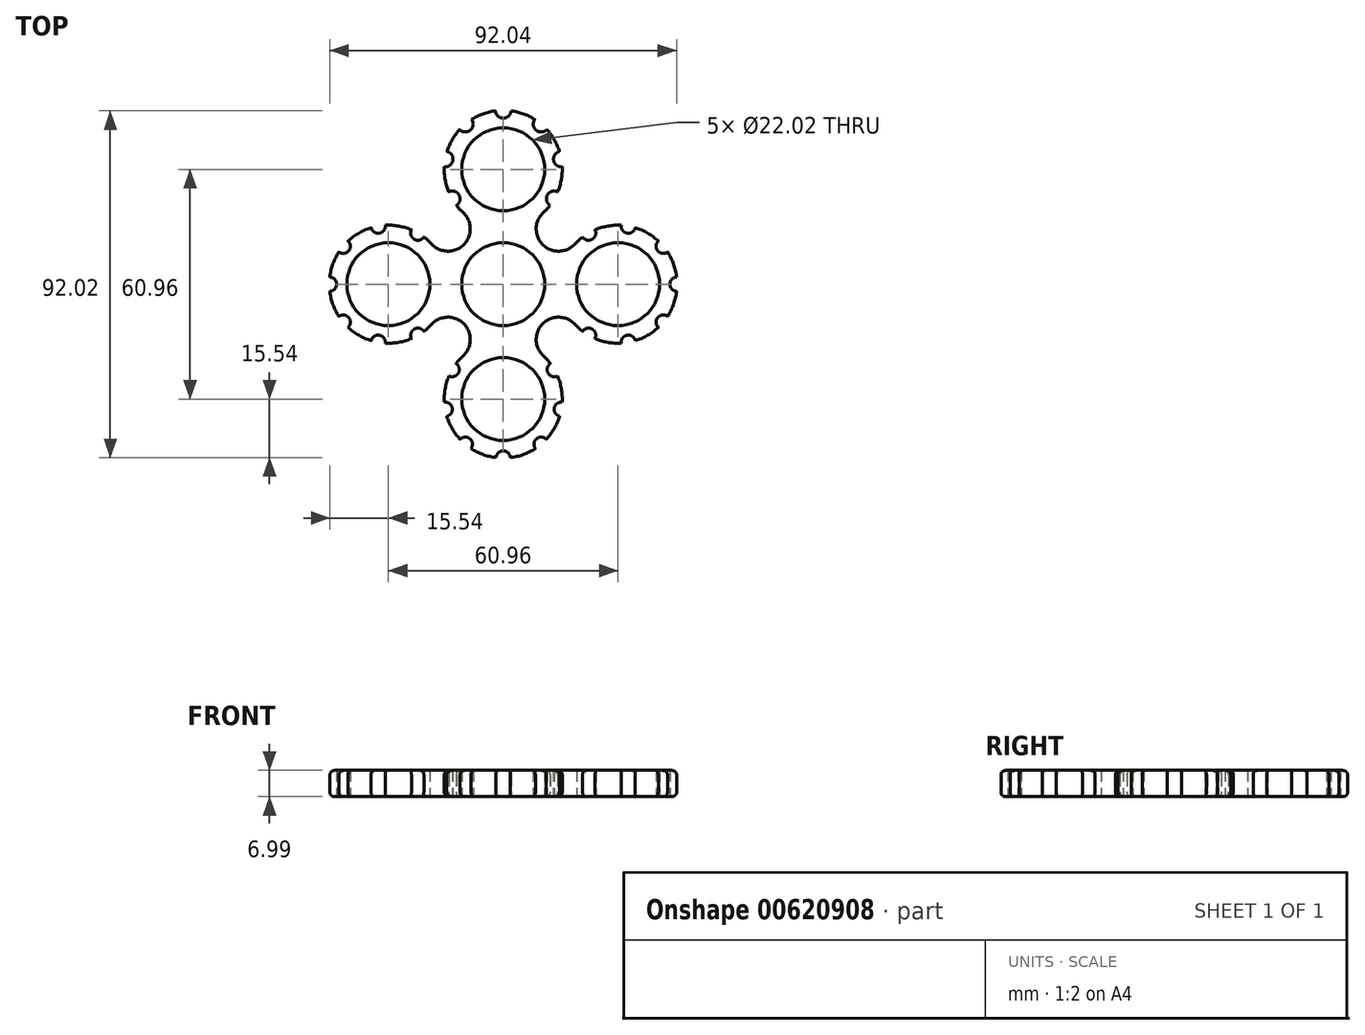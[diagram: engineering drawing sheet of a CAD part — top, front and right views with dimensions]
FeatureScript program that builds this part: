
annotation { "Feature Type Name" : "Feature", "Feature Type Description" : "" }
export const myFeature = defineFeature(function(context is Context, id is Id, definition is map)
    precondition{}
    {
        {
            var Q0;
            Q0=qCreatedBy(makeId("Top.planeOp"),FACE);
            var sketch = newSketch(context, id + "F0", { "sketchPlane" : qUnion([Q0])});
            skCircle(sketch, "E0", {"center": v(0, 0) * mm, "radius": 11.01 * mm});
            skLineSegment(sketch, "E1", {"start": v(0, 0) * mm, "end": v(30.48, 0) * mm});
            skLineSegment(sketch, "E2", {"start": v(0, 0) * mm, "end": v(0, 30.48) * mm});
            skLineSegment(sketch, "E3", {"start": v(0, 0) * mm, "end": v(0, -30.48) * mm});
            skLineSegment(sketch, "E4", {"start": v(0, 0) * mm, "end": v(-30.48, 0) * mm});
            skCircle(sketch, "E5", {"center": v(-30.48, 0) * mm, "radius": 11.01 * mm});
            skCircle(sketch, "E6", {"center": v(0, 30.48) * mm, "radius": 11.01 * mm});
            skCircle(sketch, "E7", {"center": v(0, -30.48) * mm, "radius": 11.01 * mm});
            skCircle(sketch, "E8", {"center": v(30.48, 0) * mm, "radius": 11.01 * mm});
            skCircle(sketch, "E9", {"center": v(0, 0) * mm, "radius": 14.82 * mm});
            skCircle(sketch, "E10", {"center": v(0, 30.48) * mm, "radius": 15.66 * mm});
            skCircle(sketch, "E11", {"center": v(0, -30.48) * mm, "radius": 15.66 * mm});
            skCircle(sketch, "E12", {"center": v(-30.48, 0) * mm, "radius": 15.66 * mm});
            skCircle(sketch, "E13", {"center": v(30.48, 0) * mm, "radius": 15.66 * mm});
            skCircle(sketch, "E14", {"center": v(0, 46.14) * mm, "radius": 2.08 * mm});
            skCircle(sketch, "E15.1.0", {"center": v(10.07, 42.48) * mm, "radius": 2.08 * mm});
            skCircle(sketch, "E15.2.0", {"center": v(15.42, 33.2) * mm, "radius": 2.08 * mm});
            skCircle(sketch, "E15.3.0", {"center": v(13.56, 22.65) * mm, "radius": 2.08 * mm});
            skCircle(sketch, "E15.4.0", {"center": v(5.36, 15.77) * mm, "radius": 2.08 * mm});
            skCircle(sketch, "E15.5.0", {"center": v(-5.36, 15.77) * mm, "radius": 2.08 * mm});
            skCircle(sketch, "E15.6.0", {"center": v(-13.56, 22.65) * mm, "radius": 2.08 * mm});
            skCircle(sketch, "E15.7.0", {"center": v(-15.42, 33.2) * mm, "radius": 2.08 * mm});
            skCircle(sketch, "E15.8.0", {"center": v(-10.07, 42.48) * mm, "radius": 2.08 * mm});
            skLineSegment(sketch, "E15.anchor1", {"start": v(0, 30.48) * mm, "end": v(0, 46.14) * mm, "construction": true});
            skLineSegment(sketch, "E15.anchor2", {"start": v(0, 30.48) * mm, "end": v(0, 46.14) * mm, "construction": true});
            skCircle(sketch, "E16", {"center": v(46.14, 0) * mm, "radius": 1.9 * mm});
            skCircle(sketch, "E17.1.0", {"center": v(42.48, -10.07) * mm, "radius": 1.9 * mm});
            skCircle(sketch, "E17.2.0", {"center": v(33.2, -15.42) * mm, "radius": 1.9 * mm});
            skCircle(sketch, "E17.3.0", {"center": v(22.65, -13.56) * mm, "radius": 1.9 * mm});
            skCircle(sketch, "E17.4.0", {"center": v(15.77, -5.36) * mm, "radius": 1.9 * mm});
            skCircle(sketch, "E17.5.0", {"center": v(15.77, 5.36) * mm, "radius": 1.9 * mm});
            skCircle(sketch, "E17.6.0", {"center": v(22.65, 13.56) * mm, "radius": 1.9 * mm});
            skCircle(sketch, "E17.7.0", {"center": v(33.2, 15.42) * mm, "radius": 1.9 * mm});
            skCircle(sketch, "E17.8.0", {"center": v(42.48, 10.07) * mm, "radius": 1.9 * mm});
            skLineSegment(sketch, "E17.anchor1", {"start": v(30.48, 0) * mm, "end": v(46.14, 0) * mm, "construction": true});
            skLineSegment(sketch, "E17.anchor2", {"start": v(30.48, 0) * mm, "end": v(46.14, 0) * mm, "construction": true});
            skCircle(sketch, "E18", {"center": v(-46.14, 0) * mm, "radius": 1.9 * mm});
            skCircle(sketch, "E19", {"center": v(0, -46.14) * mm, "radius": 1.9 * mm});
            skCircle(sketch, "E20.1.0", {"center": v(-42.48, 10.07) * mm, "radius": 1.9 * mm});
            skCircle(sketch, "E20.2.0", {"center": v(-33.2, 15.42) * mm, "radius": 1.9 * mm});
            skCircle(sketch, "E20.3.0", {"center": v(-22.65, 13.56) * mm, "radius": 1.9 * mm});
            skCircle(sketch, "E20.4.0", {"center": v(-15.77, 5.36) * mm, "radius": 1.9 * mm});
            skCircle(sketch, "E20.5.0", {"center": v(-15.77, -5.36) * mm, "radius": 1.9 * mm});
            skCircle(sketch, "E20.6.0", {"center": v(-22.65, -13.56) * mm, "radius": 1.9 * mm});
            skCircle(sketch, "E20.7.0", {"center": v(-33.2, -15.42) * mm, "radius": 1.9 * mm});
            skCircle(sketch, "E20.8.0", {"center": v(-42.48, -10.07) * mm, "radius": 1.9 * mm});
            skLineSegment(sketch, "E20.anchor1", {"start": v(-30.48, 0) * mm, "end": v(-46.14, 0) * mm, "construction": true});
            skLineSegment(sketch, "E20.anchor2", {"start": v(-30.48, 0) * mm, "end": v(-46.14, 0) * mm, "construction": true});
            skArc(sketch, "E21", {"start": v(-19, 10.64) * mm, "mid": v(-10.48, 10.48) * mm, "end": v(-10.64, 19) * mm});
            skArc(sketch, "E22", {"start": v(10.64, 19) * mm, "mid": v(10.48, 10.48) * mm, "end": v(19, 10.64) * mm});
            skArc(sketch, "E23", {"start": v(-10.64, -19) * mm, "mid": v(-10.48, -10.48) * mm, "end": v(-19, -10.64) * mm});
            skArc(sketch, "E24", {"start": v(19, -10.64) * mm, "mid": v(10.48, -10.48) * mm, "end": v(10.64, -19) * mm});
            skCircle(sketch, "E25.1.0", {"center": v(-10.07, -42.48) * mm, "radius": 1.9 * mm});
            skCircle(sketch, "E25.2.0", {"center": v(-15.42, -33.2) * mm, "radius": 1.9 * mm});
            skLineSegment(sketch, "E25.anchor1", {"start": v(0, -30.48) * mm, "end": v(0, -46.14) * mm, "construction": true});
            skLineSegment(sketch, "E25.anchor2", {"start": v(0, -30.48) * mm, "end": v(0, -46.14) * mm, "construction": true});
            skCircle(sketch, "E26.1.3.0", {"center": v(-13.56, -22.65) * mm, "radius": 1.9 * mm});
            skCircle(sketch, "E26.1.4.0", {"center": v(-5.36, -15.77) * mm, "radius": 1.9 * mm});
            skCircle(sketch, "E26.1.5.0", {"center": v(5.36, -15.77) * mm, "radius": 1.9 * mm});
            skCircle(sketch, "E26.1.6.0", {"center": v(13.56, -22.65) * mm, "radius": 1.9 * mm});
            skCircle(sketch, "E26.1.7.0", {"center": v(15.42, -33.2) * mm, "radius": 1.9 * mm});
            skCircle(sketch, "E26.1.8.0", {"center": v(10.07, -42.48) * mm, "radius": 1.9 * mm});
            skSolve(sketch);
        }
        {
            var Q0;
            {var subQ0=sQuery(id+"F0.wireOp",EDGE,"E22");var subQ1=sQuery(id+"F0.wireOp",EDGE,"E9");var subQ2=makeQuery(id+"F0.imprint","INTERSECT",VERTEX,{"derivedFrom":[subQ1,subQ0]});Q0=makeQuery(id+"F0.imprint","IMPRINT",FACE,{"disambiguationData":[TD([[makeQuery(id+"F0.imprint","IMPRINT",EDGE,{"disambiguationData":[TD([[subQ2,1.0]])],"derivedFrom":subQ1}),-1.0]])]});}
            var Q1;
            {var subQ0=sQuery(id+"F0.wireOp",EDGE,"E22");var subQ1=sQuery(id+"F0.wireOp",EDGE,"E9");var subQ2=makeQuery(id+"F0.imprint","INTERSECT",VERTEX,{"derivedFrom":[subQ1,subQ0]});Q1=makeQuery(id+"F0.imprint","IMPRINT",FACE,{"disambiguationData":[TD([[makeQuery(id+"F0.imprint","IMPRINT",EDGE,{"disambiguationData":[TD([[subQ2,-1.0]])],"derivedFrom":subQ1}),-1.0]])]});}
            var Q2;
            {var subQ0=sQuery(id+"F0.wireOp",EDGE,"E21");var subQ1=sQuery(id+"F0.wireOp",EDGE,"E9");var subQ2=makeQuery(id+"F0.imprint","INTERSECT",VERTEX,{"derivedFrom":[subQ1,subQ0]});Q2=makeQuery(id+"F0.imprint","IMPRINT",FACE,{"disambiguationData":[TD([[makeQuery(id+"F0.imprint","IMPRINT",EDGE,{"disambiguationData":[TD([[subQ2,1.0]])],"derivedFrom":subQ1}),-1.0]])]});}
            var Q3;
            {var subQ0=sQuery(id+"F0.wireOp",EDGE,"E21");var subQ1=sQuery(id+"F0.wireOp",EDGE,"E9");var subQ2=makeQuery(id+"F0.imprint","INTERSECT",VERTEX,{"derivedFrom":[subQ1,subQ0]});Q3=makeQuery(id+"F0.imprint","IMPRINT",FACE,{"disambiguationData":[TD([[makeQuery(id+"F0.imprint","IMPRINT",EDGE,{"disambiguationData":[TD([[subQ2,-1.0]])],"derivedFrom":subQ1}),-1.0]])]});}
            var Q4;
            {var subQ0=sQuery(id+"F0.wireOp",EDGE,"E23");var subQ1=sQuery(id+"F0.wireOp",EDGE,"E9");var subQ2=makeQuery(id+"F0.imprint","INTERSECT",VERTEX,{"derivedFrom":[subQ1,subQ0]});Q4=makeQuery(id+"F0.imprint","IMPRINT",FACE,{"disambiguationData":[TD([[makeQuery(id+"F0.imprint","IMPRINT",EDGE,{"disambiguationData":[TD([[subQ2,1.0]])],"derivedFrom":subQ1}),-1.0]])]});}
            var Q5;
            {var subQ0=sQuery(id+"F0.wireOp",EDGE,"E23");var subQ1=sQuery(id+"F0.wireOp",EDGE,"E9");var subQ2=makeQuery(id+"F0.imprint","INTERSECT",VERTEX,{"derivedFrom":[subQ1,subQ0]});Q5=makeQuery(id+"F0.imprint","IMPRINT",FACE,{"disambiguationData":[TD([[makeQuery(id+"F0.imprint","IMPRINT",EDGE,{"disambiguationData":[TD([[subQ2,-1.0]])],"derivedFrom":subQ1}),-1.0]])]});}
            var Q6;
            {var subQ0=sQuery(id+"F0.wireOp",EDGE,"E24");var subQ1=sQuery(id+"F0.wireOp",EDGE,"E9");var subQ2=makeQuery(id+"F0.imprint","INTERSECT",VERTEX,{"derivedFrom":[subQ1,subQ0]});Q6=makeQuery(id+"F0.imprint","IMPRINT",FACE,{"disambiguationData":[TD([[makeQuery(id+"F0.imprint","IMPRINT",EDGE,{"disambiguationData":[TD([[subQ2,1.0]])],"derivedFrom":subQ1}),-1.0]])]});}
            var Q7;
            {var subQ0=sQuery(id+"F0.wireOp",EDGE,"E24");var subQ1=sQuery(id+"F0.wireOp",EDGE,"E9");var subQ2=makeQuery(id+"F0.imprint","INTERSECT",VERTEX,{"derivedFrom":[subQ1,subQ0]});Q7=makeQuery(id+"F0.imprint","IMPRINT",FACE,{"disambiguationData":[TD([[makeQuery(id+"F0.imprint","IMPRINT",EDGE,{"disambiguationData":[TD([[subQ2,-1.0]])],"derivedFrom":subQ1}),-1.0]])]});}
            var Q8;
            {var subQ5=sQuery(id+"F0.wireOp",EDGE,"E0");var subQ7=sQuery(id+"F0.wireOp",EDGE,"E2");var subQ8=makeQuery(id+"F0.imprint","INTERSECT",VERTEX,{"derivedFrom":[subQ5,subQ7]});Q8=makeQuery(id+"F0.imprint","IMPRINT",FACE,{"disambiguationData":[TD([[makeQuery(id+"F0.imprint","IMPRINT",EDGE,{"disambiguationData":[TD([[subQ8,1.0]])],"derivedFrom":subQ5}),-1.0]])]});}
            var Q9;
            {var subQ3=sQuery(id+"F0.wireOp",EDGE,"E2");var subQ6=sQuery(id+"F0.wireOp",EDGE,"E0");var subQ9=makeQuery(id+"F0.imprint","INTERSECT",VERTEX,{"derivedFrom":[subQ6,subQ3]});Q9=makeQuery(id+"F0.imprint","IMPRINT",FACE,{"disambiguationData":[TD([[makeQuery(id+"F0.imprint","IMPRINT",EDGE,{"disambiguationData":[TD([[subQ9,-1.0]])],"derivedFrom":subQ6}),-1.0]])]});}
            var Q10;
            {var subQ3=sQuery(id+"F0.wireOp",EDGE,"E4");var subQ5=sQuery(id+"F0.wireOp",EDGE,"E0");var subQ6=makeQuery(id+"F0.imprint","INTERSECT",VERTEX,{"derivedFrom":[subQ5,subQ3]});Q10=makeQuery(id+"F0.imprint","IMPRINT",FACE,{"disambiguationData":[TD([[makeQuery(id+"F0.imprint","IMPRINT",EDGE,{"disambiguationData":[TD([[subQ6,-1.0]])],"derivedFrom":subQ5}),-1.0]])]});}
            var Q11;
            {var subQ6=sQuery(id+"F0.wireOp",EDGE,"E0");var subQ8=sQuery(id+"F0.wireOp",EDGE,"E1");var subQ9=makeQuery(id+"F0.imprint","INTERSECT",VERTEX,{"derivedFrom":[subQ6,subQ8]});Q11=makeQuery(id+"F0.imprint","IMPRINT",FACE,{"disambiguationData":[TD([[makeQuery(id+"F0.imprint","IMPRINT",EDGE,{"disambiguationData":[TD([[subQ9,1.0]])],"derivedFrom":subQ6}),-1.0]])]});}
            var Q12;
            Q12=makeQuery(id+"F0.imprint","IMPRINT",FACE,{"disambiguationData":[TD([[makeQuery(id+"F0.imprint","IMPRINT",EDGE,{"derivedFrom":sQuery(id+"F0.wireOp",EDGE,"E5")}),-1.0]])]});
            var Q13;
            Q13=makeQuery(id+"F0.imprint","IMPRINT",FACE,{"disambiguationData":[TD([[makeQuery(id+"F0.imprint","IMPRINT",EDGE,{"derivedFrom":sQuery(id+"F0.wireOp",EDGE,"E7")}),-1.0]])]});
            var Q14;
            Q14=makeQuery(id+"F0.imprint","IMPRINT",FACE,{"disambiguationData":[TD([[makeQuery(id+"F0.imprint","IMPRINT",EDGE,{"derivedFrom":sQuery(id+"F0.wireOp",EDGE,"E8")}),-1.0]])]});
            var Q15;
            {var subQ0=sQuery(id+"F0.wireOp",EDGE,"E20.5.0");var subQ1=sQuery(id+"F0.wireOp",EDGE,"E9");var subQ2=makeQuery(id+"F0.imprint","INTERSECT",VERTEX,{"disambiguationData":[OD(0.0)],"derivedFrom":[subQ1,subQ0]});Q15=makeQuery(id+"F0.imprint","IMPRINT",FACE,{"disambiguationData":[TD([[makeQuery(id+"F0.imprint","IMPRINT",EDGE,{"disambiguationData":[TD([[subQ2,-1.0]])],"derivedFrom":subQ1}),-1.0]])]});}
            var Q16;
            {var subQ0=sQuery(id+"F0.wireOp",EDGE,"E20.5.0");var subQ1=sQuery(id+"F0.wireOp",EDGE,"E12");var subQ2=makeQuery(id+"F0.imprint","INTERSECT",VERTEX,{"disambiguationData":[OD(0.0)],"derivedFrom":[subQ1,subQ0]});Q16=makeQuery(id+"F0.imprint","IMPRINT",FACE,{"disambiguationData":[TD([[makeQuery(id+"F0.imprint","IMPRINT",EDGE,{"disambiguationData":[TD([[subQ2,-1.0]])],"derivedFrom":subQ1}),1.0]])]});}
            var Q17;
            {var subQ0=sQuery(id+"F0.wireOp",EDGE,"E20.4.0");var subQ1=sQuery(id+"F0.wireOp",EDGE,"E9");var subQ2=makeQuery(id+"F0.imprint","INTERSECT",VERTEX,{"disambiguationData":[OD(0.0)],"derivedFrom":[subQ1,subQ0]});Q17=makeQuery(id+"F0.imprint","IMPRINT",FACE,{"disambiguationData":[TD([[makeQuery(id+"F0.imprint","IMPRINT",EDGE,{"disambiguationData":[TD([[subQ2,-1.0]])],"derivedFrom":subQ1}),-1.0]])]});}
            var Q18;
            {var subQ0=sQuery(id+"F0.wireOp",EDGE,"E20.4.0");var subQ1=sQuery(id+"F0.wireOp",EDGE,"E12");var subQ2=makeQuery(id+"F0.imprint","INTERSECT",VERTEX,{"disambiguationData":[OD(0.0)],"derivedFrom":[subQ1,subQ0]});Q18=makeQuery(id+"F0.imprint","IMPRINT",FACE,{"disambiguationData":[TD([[makeQuery(id+"F0.imprint","IMPRINT",EDGE,{"disambiguationData":[TD([[subQ2,-1.0]])],"derivedFrom":subQ1}),1.0]])]});}
            var Q19;
            {var subQ0=sQuery(id+"F0.wireOp",EDGE,"E15.5.0");var subQ1=sQuery(id+"F0.wireOp",EDGE,"E9");var subQ2=makeQuery(id+"F0.imprint","INTERSECT",VERTEX,{"disambiguationData":[OD(0.0)],"derivedFrom":[subQ1,subQ0]});Q19=makeQuery(id+"F0.imprint","IMPRINT",FACE,{"disambiguationData":[TD([[makeQuery(id+"F0.imprint","IMPRINT",EDGE,{"disambiguationData":[TD([[subQ2,-1.0]])],"derivedFrom":subQ1}),-1.0]])]});}
            var Q20;
            {var subQ0=sQuery(id+"F0.wireOp",EDGE,"E15.5.0");var subQ1=sQuery(id+"F0.wireOp",EDGE,"E10");var subQ2=makeQuery(id+"F0.imprint","INTERSECT",VERTEX,{"disambiguationData":[OD(0.0)],"derivedFrom":[subQ1,subQ0]});Q20=makeQuery(id+"F0.imprint","IMPRINT",FACE,{"disambiguationData":[TD([[makeQuery(id+"F0.imprint","IMPRINT",EDGE,{"disambiguationData":[TD([[subQ2,-1.0]])],"derivedFrom":subQ1}),1.0]])]});}
            var Q21;
            {var subQ0=sQuery(id+"F0.wireOp",EDGE,"E15.4.0");var subQ1=sQuery(id+"F0.wireOp",EDGE,"E9");var subQ2=makeQuery(id+"F0.imprint","INTERSECT",VERTEX,{"disambiguationData":[OD(0.0)],"derivedFrom":[subQ1,subQ0]});Q21=makeQuery(id+"F0.imprint","IMPRINT",FACE,{"disambiguationData":[TD([[makeQuery(id+"F0.imprint","IMPRINT",EDGE,{"disambiguationData":[TD([[subQ2,-1.0]])],"derivedFrom":subQ1}),-1.0]])]});}
            var Q22;
            {var subQ0=sQuery(id+"F0.wireOp",EDGE,"E15.4.0");var subQ1=sQuery(id+"F0.wireOp",EDGE,"E10");var subQ2=makeQuery(id+"F0.imprint","INTERSECT",VERTEX,{"disambiguationData":[OD(0.0)],"derivedFrom":[subQ1,subQ0]});Q22=makeQuery(id+"F0.imprint","IMPRINT",FACE,{"disambiguationData":[TD([[makeQuery(id+"F0.imprint","IMPRINT",EDGE,{"disambiguationData":[TD([[subQ2,-1.0]])],"derivedFrom":subQ1}),1.0]])]});}
            var Q23;
            {var subQ0=sQuery(id+"F0.wireOp",EDGE,"E17.5.0");var subQ1=sQuery(id+"F0.wireOp",EDGE,"E13");var subQ2=makeQuery(id+"F0.imprint","INTERSECT",VERTEX,{"disambiguationData":[OD(0.0)],"derivedFrom":[subQ1,subQ0]});Q23=makeQuery(id+"F0.imprint","IMPRINT",FACE,{"disambiguationData":[TD([[makeQuery(id+"F0.imprint","IMPRINT",EDGE,{"disambiguationData":[TD([[subQ2,-1.0]])],"derivedFrom":subQ1}),1.0]])]});}
            var Q24;
            {var subQ0=sQuery(id+"F0.wireOp",EDGE,"E17.5.0");var subQ1=sQuery(id+"F0.wireOp",EDGE,"E9");var subQ2=makeQuery(id+"F0.imprint","INTERSECT",VERTEX,{"disambiguationData":[OD(0.0)],"derivedFrom":[subQ1,subQ0]});Q24=makeQuery(id+"F0.imprint","IMPRINT",FACE,{"disambiguationData":[TD([[makeQuery(id+"F0.imprint","IMPRINT",EDGE,{"disambiguationData":[TD([[subQ2,-1.0]])],"derivedFrom":subQ1}),-1.0]])]});}
            var Q25;
            {var subQ0=sQuery(id+"F0.wireOp",EDGE,"E17.4.0");var subQ1=sQuery(id+"F0.wireOp",EDGE,"E13");var subQ2=makeQuery(id+"F0.imprint","INTERSECT",VERTEX,{"disambiguationData":[OD(0.0)],"derivedFrom":[subQ1,subQ0]});Q25=makeQuery(id+"F0.imprint","IMPRINT",FACE,{"disambiguationData":[TD([[makeQuery(id+"F0.imprint","IMPRINT",EDGE,{"disambiguationData":[TD([[subQ2,-1.0]])],"derivedFrom":subQ1}),1.0]])]});}
            var Q26;
            {var subQ0=sQuery(id+"F0.wireOp",EDGE,"E17.4.0");var subQ1=sQuery(id+"F0.wireOp",EDGE,"E9");var subQ2=makeQuery(id+"F0.imprint","INTERSECT",VERTEX,{"disambiguationData":[OD(0.0)],"derivedFrom":[subQ1,subQ0]});Q26=makeQuery(id+"F0.imprint","IMPRINT",FACE,{"disambiguationData":[TD([[makeQuery(id+"F0.imprint","IMPRINT",EDGE,{"disambiguationData":[TD([[subQ2,-1.0]])],"derivedFrom":subQ1}),-1.0]])]});}
            var Q27;
            {var subQ0=sQuery(id+"F0.wireOp",EDGE,"E26.1.5.0");var subQ1=sQuery(id+"F0.wireOp",EDGE,"E11");var subQ2=makeQuery(id+"F0.imprint","INTERSECT",VERTEX,{"disambiguationData":[OD(0.0)],"derivedFrom":[subQ1,subQ0]});Q27=makeQuery(id+"F0.imprint","IMPRINT",FACE,{"disambiguationData":[TD([[makeQuery(id+"F0.imprint","IMPRINT",EDGE,{"disambiguationData":[TD([[subQ2,-1.0]])],"derivedFrom":subQ1}),1.0]])]});}
            var Q28;
            {var subQ0=sQuery(id+"F0.wireOp",EDGE,"E26.1.4.0");var subQ1=sQuery(id+"F0.wireOp",EDGE,"E9");var subQ2=makeQuery(id+"F0.imprint","INTERSECT",VERTEX,{"disambiguationData":[OD(0.0)],"derivedFrom":[subQ1,subQ0]});Q28=makeQuery(id+"F0.imprint","IMPRINT",FACE,{"disambiguationData":[TD([[makeQuery(id+"F0.imprint","IMPRINT",EDGE,{"disambiguationData":[TD([[subQ2,-1.0]])],"derivedFrom":subQ1}),-1.0]])]});}
            var Q29;
            {var subQ0=sQuery(id+"F0.wireOp",EDGE,"E26.1.4.0");var subQ1=sQuery(id+"F0.wireOp",EDGE,"E11");var subQ2=makeQuery(id+"F0.imprint","INTERSECT",VERTEX,{"disambiguationData":[OD(0.0)],"derivedFrom":[subQ1,subQ0]});Q29=makeQuery(id+"F0.imprint","IMPRINT",FACE,{"disambiguationData":[TD([[makeQuery(id+"F0.imprint","IMPRINT",EDGE,{"disambiguationData":[TD([[subQ2,-1.0]])],"derivedFrom":subQ1}),1.0]])]});}
            var Q30;
            {var subQ0=sQuery(id+"F0.wireOp",EDGE,"E17.5.0");var subQ1=sQuery(id+"F0.wireOp",EDGE,"E9");var subQ2=makeQuery(id+"F0.imprint","INTERSECT",VERTEX,{"disambiguationData":[OD(0.0)],"derivedFrom":[subQ1,subQ0]});Q30=makeQuery(id+"F0.imprint","IMPRINT",FACE,{"disambiguationData":[TD([[makeQuery(id+"F0.imprint","IMPRINT",EDGE,{"disambiguationData":[TD([[subQ2,-1.0]])],"derivedFrom":subQ0}),-1.0]])]});}
            var Q31;
            {var subQ0=sQuery(id+"F0.wireOp",EDGE,"E17.4.0");var subQ1=sQuery(id+"F0.wireOp",EDGE,"E9");var subQ2=makeQuery(id+"F0.imprint","INTERSECT",VERTEX,{"disambiguationData":[OD(1.0)],"derivedFrom":[subQ1,subQ0]});Q31=makeQuery(id+"F0.imprint","IMPRINT",FACE,{"disambiguationData":[TD([[makeQuery(id+"F0.imprint","IMPRINT",EDGE,{"disambiguationData":[TD([[subQ2,1.0]])],"derivedFrom":subQ0}),-1.0]])]});}
            var Q32;
            {var subQ0=sQuery(id+"F0.wireOp",EDGE,"E17.4.0");var subQ1=sQuery(id+"F0.wireOp",EDGE,"E9");var subQ2=makeQuery(id+"F0.imprint","INTERSECT",VERTEX,{"disambiguationData":[OD(0.0)],"derivedFrom":[subQ1,subQ0]});Q32=makeQuery(id+"F0.imprint","IMPRINT",FACE,{"disambiguationData":[TD([[makeQuery(id+"F0.imprint","IMPRINT",EDGE,{"disambiguationData":[TD([[subQ2,-1.0]])],"derivedFrom":subQ1}),1.0]])]});}
            var Q33;
            {var subQ0=sQuery(id+"F0.wireOp",EDGE,"E17.5.0");var subQ1=sQuery(id+"F0.wireOp",EDGE,"E9");var subQ2=makeQuery(id+"F0.imprint","INTERSECT",VERTEX,{"disambiguationData":[OD(0.0)],"derivedFrom":[subQ1,subQ0]});Q33=makeQuery(id+"F0.imprint","IMPRINT",FACE,{"disambiguationData":[TD([[makeQuery(id+"F0.imprint","IMPRINT",EDGE,{"disambiguationData":[TD([[subQ2,-1.0]])],"derivedFrom":subQ1}),1.0]])]});}
            var Q34;
            {var subQ0=sQuery(id+"F0.wireOp",EDGE,"E15.4.0");var subQ1=sQuery(id+"F0.wireOp",EDGE,"E9");var subQ2=makeQuery(id+"F0.imprint","INTERSECT",VERTEX,{"disambiguationData":[OD(0.0)],"derivedFrom":[subQ1,subQ0]});Q34=makeQuery(id+"F0.imprint","IMPRINT",FACE,{"disambiguationData":[TD([[makeQuery(id+"F0.imprint","IMPRINT",EDGE,{"disambiguationData":[TD([[subQ2,-1.0]])],"derivedFrom":subQ1}),1.0]])]});}
            var Q35;
            {var subQ0=sQuery(id+"F0.wireOp",EDGE,"E15.4.0");var subQ1=sQuery(id+"F0.wireOp",EDGE,"E9");var subQ2=makeQuery(id+"F0.imprint","INTERSECT",VERTEX,{"disambiguationData":[OD(1.0)],"derivedFrom":[subQ1,subQ0]});Q35=makeQuery(id+"F0.imprint","IMPRINT",FACE,{"disambiguationData":[TD([[makeQuery(id+"F0.imprint","IMPRINT",EDGE,{"disambiguationData":[TD([[subQ2,1.0]])],"derivedFrom":subQ0}),-1.0]])]});}
            var Q36;
            {var subQ0=sQuery(id+"F0.wireOp",EDGE,"E15.5.0");var subQ1=sQuery(id+"F0.wireOp",EDGE,"E9");var subQ2=makeQuery(id+"F0.imprint","INTERSECT",VERTEX,{"disambiguationData":[OD(0.0)],"derivedFrom":[subQ1,subQ0]});Q36=makeQuery(id+"F0.imprint","IMPRINT",FACE,{"disambiguationData":[TD([[makeQuery(id+"F0.imprint","IMPRINT",EDGE,{"disambiguationData":[TD([[subQ2,-1.0]])],"derivedFrom":subQ0}),-1.0]])]});}
            var Q37;
            {var subQ0=sQuery(id+"F0.wireOp",EDGE,"E15.5.0");var subQ1=sQuery(id+"F0.wireOp",EDGE,"E9");var subQ2=makeQuery(id+"F0.imprint","INTERSECT",VERTEX,{"disambiguationData":[OD(0.0)],"derivedFrom":[subQ1,subQ0]});Q37=makeQuery(id+"F0.imprint","IMPRINT",FACE,{"disambiguationData":[TD([[makeQuery(id+"F0.imprint","IMPRINT",EDGE,{"disambiguationData":[TD([[subQ2,-1.0]])],"derivedFrom":subQ1}),1.0]])]});}
            var Q38;
            {var subQ0=sQuery(id+"F0.wireOp",EDGE,"E26.1.5.0");var subQ1=sQuery(id+"F0.wireOp",EDGE,"E9");var subQ2=makeQuery(id+"F0.imprint","INTERSECT",VERTEX,{"disambiguationData":[OD(0.0)],"derivedFrom":[subQ1,subQ0]});Q38=makeQuery(id+"F0.imprint","IMPRINT",FACE,{"disambiguationData":[TD([[makeQuery(id+"F0.imprint","IMPRINT",EDGE,{"disambiguationData":[TD([[subQ2,-1.0]])],"derivedFrom":subQ1}),-1.0]])]});}
            var Q39;
            {var subQ0=sQuery(id+"F0.wireOp",EDGE,"E26.1.5.0");var subQ1=sQuery(id+"F0.wireOp",EDGE,"E9");var subQ2=makeQuery(id+"F0.imprint","INTERSECT",VERTEX,{"disambiguationData":[OD(0.0)],"derivedFrom":[subQ1,subQ0]});Q39=makeQuery(id+"F0.imprint","IMPRINT",FACE,{"disambiguationData":[TD([[makeQuery(id+"F0.imprint","IMPRINT",EDGE,{"disambiguationData":[TD([[subQ2,-1.0]])],"derivedFrom":subQ0}),-1.0]])]});}
            var Q40;
            {var subQ0=sQuery(id+"F0.wireOp",EDGE,"E26.1.4.0");var subQ1=sQuery(id+"F0.wireOp",EDGE,"E9");var subQ2=makeQuery(id+"F0.imprint","INTERSECT",VERTEX,{"disambiguationData":[OD(1.0)],"derivedFrom":[subQ1,subQ0]});Q40=makeQuery(id+"F0.imprint","IMPRINT",FACE,{"disambiguationData":[TD([[makeQuery(id+"F0.imprint","IMPRINT",EDGE,{"disambiguationData":[TD([[subQ2,1.0]])],"derivedFrom":subQ0}),-1.0]])]});}
            var Q41;
            {var subQ0=sQuery(id+"F0.wireOp",EDGE,"E26.1.4.0");var subQ1=sQuery(id+"F0.wireOp",EDGE,"E9");var subQ2=makeQuery(id+"F0.imprint","INTERSECT",VERTEX,{"disambiguationData":[OD(0.0)],"derivedFrom":[subQ1,subQ0]});Q41=makeQuery(id+"F0.imprint","IMPRINT",FACE,{"disambiguationData":[TD([[makeQuery(id+"F0.imprint","IMPRINT",EDGE,{"disambiguationData":[TD([[subQ2,-1.0]])],"derivedFrom":subQ1}),1.0]])]});}
            var Q42;
            {var subQ0=sQuery(id+"F0.wireOp",EDGE,"E26.1.5.0");var subQ1=sQuery(id+"F0.wireOp",EDGE,"E9");var subQ2=makeQuery(id+"F0.imprint","INTERSECT",VERTEX,{"disambiguationData":[OD(0.0)],"derivedFrom":[subQ1,subQ0]});Q42=makeQuery(id+"F0.imprint","IMPRINT",FACE,{"disambiguationData":[TD([[makeQuery(id+"F0.imprint","IMPRINT",EDGE,{"disambiguationData":[TD([[subQ2,-1.0]])],"derivedFrom":subQ1}),1.0]])]});}
            var Q43;
            {var subQ0=sQuery(id+"F0.wireOp",EDGE,"E20.4.0");var subQ1=sQuery(id+"F0.wireOp",EDGE,"E9");var subQ2=makeQuery(id+"F0.imprint","INTERSECT",VERTEX,{"disambiguationData":[OD(1.0)],"derivedFrom":[subQ1,subQ0]});Q43=makeQuery(id+"F0.imprint","IMPRINT",FACE,{"disambiguationData":[TD([[makeQuery(id+"F0.imprint","IMPRINT",EDGE,{"disambiguationData":[TD([[subQ2,1.0]])],"derivedFrom":subQ0}),-1.0]])]});}
            var Q44;
            {var subQ0=sQuery(id+"F0.wireOp",EDGE,"E20.5.0");var subQ1=sQuery(id+"F0.wireOp",EDGE,"E9");var subQ2=makeQuery(id+"F0.imprint","INTERSECT",VERTEX,{"disambiguationData":[OD(0.0)],"derivedFrom":[subQ1,subQ0]});Q44=makeQuery(id+"F0.imprint","IMPRINT",FACE,{"disambiguationData":[TD([[makeQuery(id+"F0.imprint","IMPRINT",EDGE,{"disambiguationData":[TD([[subQ2,-1.0]])],"derivedFrom":subQ0}),-1.0]])]});}
            var Q45;
            {var subQ0=sQuery(id+"F0.wireOp",EDGE,"E20.5.0");var subQ1=sQuery(id+"F0.wireOp",EDGE,"E9");var subQ2=makeQuery(id+"F0.imprint","INTERSECT",VERTEX,{"disambiguationData":[OD(0.0)],"derivedFrom":[subQ1,subQ0]});Q45=makeQuery(id+"F0.imprint","IMPRINT",FACE,{"disambiguationData":[TD([[makeQuery(id+"F0.imprint","IMPRINT",EDGE,{"disambiguationData":[TD([[subQ2,-1.0]])],"derivedFrom":subQ1}),1.0]])]});}
            var Q46;
            {var subQ0=sQuery(id+"F0.wireOp",EDGE,"E20.4.0");var subQ1=sQuery(id+"F0.wireOp",EDGE,"E9");var subQ2=makeQuery(id+"F0.imprint","INTERSECT",VERTEX,{"disambiguationData":[OD(0.0)],"derivedFrom":[subQ1,subQ0]});Q46=makeQuery(id+"F0.imprint","IMPRINT",FACE,{"disambiguationData":[TD([[makeQuery(id+"F0.imprint","IMPRINT",EDGE,{"disambiguationData":[TD([[subQ2,-1.0]])],"derivedFrom":subQ1}),1.0]])]});}
            var Q47;
            Q47=makeQuery(id+"F0.imprint","IMPRINT",FACE,{"disambiguationData":[TD([[makeQuery(id+"F0.imprint","IMPRINT",EDGE,{"derivedFrom":sQuery(id+"F0.wireOp",EDGE,"E6")}),-1.0]])]});
            extrude(context, id + "F1", {"entities" : qUnion([Q0, Q1, Q2, Q3, Q4, Q5, Q6, Q7, Q8, Q9, Q10, Q11, Q12, Q13, Q14, Q15, Q16, Q17, Q18, Q19, Q20, Q21, Q22, Q23, Q24, Q25, Q26, Q27, Q28, Q29, Q30, Q31, Q32, Q33, Q34, Q35, Q36, Q37, Q38, Q39, Q40, Q41, Q42, Q43, Q44, Q45, Q46, Q47]), "depth" : 7 * mm, "offsetDistance" : 25.4 * mm});
        }
        {
            var Q0;
            Q0=makeQuery(id+"F1.opExtrude","CAP_EDGE",EDGE,{"disambiguationData":[OSD([sQuery(id+"F0.wireOp",EDGE,"E21")])],"isStart":false});
            var Q1;
            {var subQ0=sQuery(id+"F0.wireOp",EDGE,"E10");Q1=makeQuery(id+"F1.opExtrude","CAP_EDGE",EDGE,{"disambiguationData":[OSD([subQ0]),TDD([makeQuery(id+"F0.imprint","IMPRINT",EDGE,{"disambiguationData":[TD([[makeQuery(id+"F0.imprint","INTERSECT",VERTEX,{"disambiguationData":[OD(1.0)],"derivedFrom":[subQ0,sQuery(id+"F0.wireOp",EDGE,"E15.7.0")]}),-1.0]])],"derivedFrom":subQ0})])],"isStart":false});}
            var Q2;
            {var subQ0=sQuery(id+"F0.wireOp",EDGE,"E10");Q2=makeQuery(id+"F1.opExtrude","CAP_EDGE",EDGE,{"disambiguationData":[OSD([subQ0]),TDD([makeQuery(id+"F0.imprint","IMPRINT",EDGE,{"disambiguationData":[TD([[makeQuery(id+"F0.imprint","INTERSECT",VERTEX,{"disambiguationData":[OD(1.0)],"derivedFrom":[subQ0,sQuery(id+"F0.wireOp",EDGE,"E15.8.0")]}),-1.0]])],"derivedFrom":subQ0})])],"isStart":false});}
            var Q3;
            {var subQ0=sQuery(id+"F0.wireOp",EDGE,"E10");Q3=makeQuery(id+"F1.opExtrude","CAP_EDGE",EDGE,{"disambiguationData":[OSD([subQ0]),TDD([makeQuery(id+"F0.imprint","IMPRINT",EDGE,{"disambiguationData":[TD([[makeQuery(id+"F0.imprint","INTERSECT",VERTEX,{"disambiguationData":[OD(1.0)],"derivedFrom":[subQ0,sQuery(id+"F0.wireOp",EDGE,"E14")]}),-1.0]])],"derivedFrom":subQ0})])],"isStart":false});}
            var Q4;
            {var subQ0=sQuery(id+"F0.wireOp",EDGE,"E10");Q4=makeQuery(id+"F1.opExtrude","CAP_EDGE",EDGE,{"disambiguationData":[OSD([subQ0]),TDD([makeQuery(id+"F0.imprint","IMPRINT",EDGE,{"disambiguationData":[TD([[makeQuery(id+"F0.imprint","INTERSECT",VERTEX,{"disambiguationData":[OD(1.0)],"derivedFrom":[subQ0,sQuery(id+"F0.wireOp",EDGE,"E15.1.0")]}),-1.0]])],"derivedFrom":subQ0})])],"isStart":false});}
            var Q5;
            {var subQ0=sQuery(id+"F0.wireOp",EDGE,"E10");Q5=makeQuery(id+"F1.opExtrude","CAP_EDGE",EDGE,{"disambiguationData":[OSD([subQ0]),TDD([makeQuery(id+"F0.imprint","IMPRINT",EDGE,{"disambiguationData":[TD([[makeQuery(id+"F0.imprint","INTERSECT",VERTEX,{"disambiguationData":[OD(0.0)],"derivedFrom":[subQ0,sQuery(id+"F0.wireOp",EDGE,"E15.2.0")]}),-1.0]])],"derivedFrom":subQ0})])],"isStart":false});}
            var Q6;
            {var subQ0=sQuery(id+"F0.wireOp",EDGE,"E10");Q6=makeQuery(id+"F1.opExtrude","CAP_EDGE",EDGE,{"disambiguationData":[OSD([subQ0]),TDD([makeQuery(id+"F0.imprint","IMPRINT",EDGE,{"disambiguationData":[TD([[makeQuery(id+"F0.imprint","INTERSECT",VERTEX,{"disambiguationData":[OD(1.0)],"derivedFrom":[subQ0,sQuery(id+"F0.wireOp",EDGE,"E15.2.0")]}),1.0]])],"derivedFrom":subQ0})])],"isStart":false});}
            var Q7;
            Q7=makeQuery(id+"F1.opExtrude","CAP_EDGE",EDGE,{"disambiguationData":[OSD([sQuery(id+"F0.wireOp",EDGE,"E22")])],"isStart":false});
            var Q8;
            {var subQ0=sQuery(id+"F0.wireOp",EDGE,"E13");Q8=makeQuery(id+"F1.opExtrude","CAP_EDGE",EDGE,{"disambiguationData":[OSD([subQ0]),TDD([makeQuery(id+"F0.imprint","IMPRINT",EDGE,{"disambiguationData":[TD([[makeQuery(id+"F0.imprint","INTERSECT",VERTEX,{"disambiguationData":[OD(1.0)],"derivedFrom":[subQ0,sQuery(id+"F0.wireOp",EDGE,"E17.7.0")]}),-1.0]])],"derivedFrom":subQ0})])],"isStart":false});}
            var Q9;
            {var subQ0=sQuery(id+"F0.wireOp",EDGE,"E13");Q9=makeQuery(id+"F1.opExtrude","CAP_EDGE",EDGE,{"disambiguationData":[OSD([subQ0]),TDD([makeQuery(id+"F0.imprint","IMPRINT",EDGE,{"disambiguationData":[TD([[makeQuery(id+"F0.imprint","INTERSECT",VERTEX,{"disambiguationData":[OD(1.0)],"derivedFrom":[subQ0,sQuery(id+"F0.wireOp",EDGE,"E17.8.0")]}),-1.0]])],"derivedFrom":subQ0})])],"isStart":false});}
            var Q10;
            {var subQ0=sQuery(id+"F0.wireOp",EDGE,"E13");Q10=makeQuery(id+"F1.opExtrude","CAP_EDGE",EDGE,{"disambiguationData":[OSD([subQ0]),TDD([makeQuery(id+"F0.imprint","IMPRINT",EDGE,{"disambiguationData":[TD([[makeQuery(id+"F0.imprint","INTERSECT",VERTEX,{"disambiguationData":[OD(0.0)],"derivedFrom":[subQ0,sQuery(id+"F0.wireOp",EDGE,"E17.8.0")]}),1.0]])],"derivedFrom":subQ0})])],"isStart":false});}
            var Q11;
            {var subQ0=sQuery(id+"F0.wireOp",EDGE,"E13");Q11=makeQuery(id+"F1.opExtrude","CAP_EDGE",EDGE,{"disambiguationData":[OSD([subQ0]),TDD([makeQuery(id+"F0.imprint","IMPRINT",EDGE,{"disambiguationData":[TD([[makeQuery(id+"F0.imprint","INTERSECT",VERTEX,{"disambiguationData":[OD(1.0)],"derivedFrom":[subQ0,sQuery(id+"F0.wireOp",EDGE,"E17.1.0")]}),-1.0]])],"derivedFrom":subQ0})])],"isStart":false});}
            var Q12;
            {var subQ0=sQuery(id+"F0.wireOp",EDGE,"E13");Q12=makeQuery(id+"F1.opExtrude","CAP_EDGE",EDGE,{"disambiguationData":[OSD([subQ0]),TDD([makeQuery(id+"F0.imprint","IMPRINT",EDGE,{"disambiguationData":[TD([[makeQuery(id+"F0.imprint","INTERSECT",VERTEX,{"disambiguationData":[OD(1.0)],"derivedFrom":[subQ0,sQuery(id+"F0.wireOp",EDGE,"E17.2.0")]}),-1.0]])],"derivedFrom":subQ0})])],"isStart":false});}
            var Q13;
            {var subQ0=sQuery(id+"F0.wireOp",EDGE,"E13");Q13=makeQuery(id+"F1.opExtrude","CAP_EDGE",EDGE,{"disambiguationData":[OSD([subQ0]),TDD([makeQuery(id+"F0.imprint","IMPRINT",EDGE,{"disambiguationData":[TD([[makeQuery(id+"F0.imprint","INTERSECT",VERTEX,{"disambiguationData":[OD(1.0)],"derivedFrom":[subQ0,sQuery(id+"F0.wireOp",EDGE,"E17.3.0")]}),-1.0]])],"derivedFrom":subQ0})])],"isStart":false});}
            var Q14;
            Q14=makeQuery(id+"F1.opExtrude","CAP_EDGE",EDGE,{"disambiguationData":[OSD([sQuery(id+"F0.wireOp",EDGE,"E24")])],"isStart":false});
            var Q15;
            {var subQ0=sQuery(id+"F0.wireOp",EDGE,"E11");Q15=makeQuery(id+"F1.opExtrude","CAP_EDGE",EDGE,{"disambiguationData":[OSD([subQ0]),TDD([makeQuery(id+"F0.imprint","IMPRINT",EDGE,{"disambiguationData":[TD([[makeQuery(id+"F0.imprint","INTERSECT",VERTEX,{"disambiguationData":[OD(1.0)],"derivedFrom":[subQ0,sQuery(id+"F0.wireOp",EDGE,"E26.1.6.0")]}),1.0]])],"derivedFrom":subQ0})])],"isStart":false});}
            var Q16;
            {var subQ0=sQuery(id+"F0.wireOp",EDGE,"E11");Q16=makeQuery(id+"F1.opExtrude","CAP_EDGE",EDGE,{"disambiguationData":[OSD([subQ0]),TDD([makeQuery(id+"F0.imprint","IMPRINT",EDGE,{"disambiguationData":[TD([[makeQuery(id+"F0.imprint","INTERSECT",VERTEX,{"disambiguationData":[OD(1.0)],"derivedFrom":[subQ0,sQuery(id+"F0.wireOp",EDGE,"E26.1.8.0")]}),-1.0]])],"derivedFrom":subQ0})])],"isStart":false});}
            var Q17;
            {var subQ0=sQuery(id+"F0.wireOp",EDGE,"E11");Q17=makeQuery(id+"F1.opExtrude","CAP_EDGE",EDGE,{"disambiguationData":[OSD([subQ0]),TDD([makeQuery(id+"F0.imprint","IMPRINT",EDGE,{"disambiguationData":[TD([[makeQuery(id+"F0.imprint","INTERSECT",VERTEX,{"disambiguationData":[OD(1.0)],"derivedFrom":[subQ0,sQuery(id+"F0.wireOp",EDGE,"E19")]}),-1.0]])],"derivedFrom":subQ0})])],"isStart":false});}
            var Q18;
            {var subQ0=sQuery(id+"F0.wireOp",EDGE,"E11");Q18=makeQuery(id+"F1.opExtrude","CAP_EDGE",EDGE,{"disambiguationData":[OSD([subQ0]),TDD([makeQuery(id+"F0.imprint","IMPRINT",EDGE,{"disambiguationData":[TD([[makeQuery(id+"F0.imprint","INTERSECT",VERTEX,{"disambiguationData":[OD(1.0)],"derivedFrom":[subQ0,sQuery(id+"F0.wireOp",EDGE,"E25.1.0")]}),-1.0]])],"derivedFrom":subQ0})])],"isStart":false});}
            var Q19;
            {var subQ0=sQuery(id+"F0.wireOp",EDGE,"E11");Q19=makeQuery(id+"F1.opExtrude","CAP_EDGE",EDGE,{"disambiguationData":[OSD([subQ0]),TDD([makeQuery(id+"F0.imprint","IMPRINT",EDGE,{"disambiguationData":[TD([[makeQuery(id+"F0.imprint","INTERSECT",VERTEX,{"disambiguationData":[OD(1.0)],"derivedFrom":[subQ0,sQuery(id+"F0.wireOp",EDGE,"E25.2.0")]}),-1.0]])],"derivedFrom":subQ0})])],"isStart":false});}
            var Q20;
            {var subQ0=sQuery(id+"F0.wireOp",EDGE,"E11");Q20=makeQuery(id+"F1.opExtrude","CAP_EDGE",EDGE,{"disambiguationData":[OSD([subQ0]),TDD([makeQuery(id+"F0.imprint","IMPRINT",EDGE,{"disambiguationData":[TD([[makeQuery(id+"F0.imprint","INTERSECT",VERTEX,{"disambiguationData":[OD(1.0)],"derivedFrom":[subQ0,sQuery(id+"F0.wireOp",EDGE,"E26.1.3.0")]}),-1.0]])],"derivedFrom":subQ0})])],"isStart":false});}
            var Q21;
            Q21=makeQuery(id+"F1.opExtrude","CAP_EDGE",EDGE,{"disambiguationData":[OSD([sQuery(id+"F0.wireOp",EDGE,"E23")])],"isStart":false});
            var Q22;
            {var subQ0=sQuery(id+"F0.wireOp",EDGE,"E12");Q22=makeQuery(id+"F1.opExtrude","CAP_EDGE",EDGE,{"disambiguationData":[OSD([subQ0]),TDD([makeQuery(id+"F0.imprint","IMPRINT",EDGE,{"disambiguationData":[TD([[makeQuery(id+"F0.imprint","INTERSECT",VERTEX,{"disambiguationData":[OD(1.0)],"derivedFrom":[subQ0,sQuery(id+"F0.wireOp",EDGE,"E20.7.0")]}),-1.0]])],"derivedFrom":subQ0})])],"isStart":false});}
            var Q23;
            {var subQ0=sQuery(id+"F0.wireOp",EDGE,"E12");Q23=makeQuery(id+"F1.opExtrude","CAP_EDGE",EDGE,{"disambiguationData":[OSD([subQ0]),TDD([makeQuery(id+"F0.imprint","IMPRINT",EDGE,{"disambiguationData":[TD([[makeQuery(id+"F0.imprint","INTERSECT",VERTEX,{"disambiguationData":[OD(1.0)],"derivedFrom":[subQ0,sQuery(id+"F0.wireOp",EDGE,"E20.8.0")]}),-1.0]])],"derivedFrom":subQ0})])],"isStart":false});}
            var Q24;
            {var subQ0=sQuery(id+"F0.wireOp",EDGE,"E12");Q24=makeQuery(id+"F1.opExtrude","CAP_EDGE",EDGE,{"disambiguationData":[OSD([subQ0]),TDD([makeQuery(id+"F0.imprint","IMPRINT",EDGE,{"disambiguationData":[TD([[makeQuery(id+"F0.imprint","INTERSECT",VERTEX,{"disambiguationData":[OD(1.0)],"derivedFrom":[subQ0,sQuery(id+"F0.wireOp",EDGE,"E18")]}),-1.0]])],"derivedFrom":subQ0})])],"isStart":false});}
            var Q25;
            {var subQ0=sQuery(id+"F0.wireOp",EDGE,"E12");Q25=makeQuery(id+"F1.opExtrude","CAP_EDGE",EDGE,{"disambiguationData":[OSD([subQ0]),TDD([makeQuery(id+"F0.imprint","IMPRINT",EDGE,{"disambiguationData":[TD([[makeQuery(id+"F0.imprint","INTERSECT",VERTEX,{"disambiguationData":[OD(1.0)],"derivedFrom":[subQ0,sQuery(id+"F0.wireOp",EDGE,"E20.1.0")]}),-1.0]])],"derivedFrom":subQ0})])],"isStart":false});}
            var Q26;
            {var subQ0=sQuery(id+"F0.wireOp",EDGE,"E12");Q26=makeQuery(id+"F1.opExtrude","CAP_EDGE",EDGE,{"disambiguationData":[OSD([subQ0]),TDD([makeQuery(id+"F0.imprint","IMPRINT",EDGE,{"disambiguationData":[TD([[makeQuery(id+"F0.imprint","INTERSECT",VERTEX,{"disambiguationData":[OD(1.0)],"derivedFrom":[subQ0,sQuery(id+"F0.wireOp",EDGE,"E20.2.0")]}),-1.0]])],"derivedFrom":subQ0})])],"isStart":false});}
            var Q27;
            {var subQ0=sQuery(id+"F0.wireOp",EDGE,"E12");Q27=makeQuery(id+"F1.opExtrude","CAP_EDGE",EDGE,{"disambiguationData":[OSD([subQ0]),TDD([makeQuery(id+"F0.imprint","IMPRINT",EDGE,{"disambiguationData":[TD([[makeQuery(id+"F0.imprint","INTERSECT",VERTEX,{"disambiguationData":[OD(1.0)],"derivedFrom":[subQ0,sQuery(id+"F0.wireOp",EDGE,"E20.3.0")]}),-1.0]])],"derivedFrom":subQ0})])],"isStart":false});}
            fillet(context, id + "F2", {"entities" : qUnion([Q0, Q1, Q2, Q3, Q4, Q5, Q6, Q7, Q8, Q9, Q10, Q11, Q12, Q13, Q14, Q15, Q16, Q17, Q18, Q19, Q20, Q21, Q22, Q23, Q24, Q25, Q26, Q27]), "radius" : 1.27 * mm, "tangentPropagation" : true, "allowEdgeOverflow" : false});
        }
        {
            var Q0;
            Q0=makeQuery(id+"F1.opExtrude","CAP_EDGE",EDGE,{"disambiguationData":[OSD([sQuery(id+"F0.wireOp",EDGE,"E23")])],"isStart":true});
            var Q1;
            {var subQ0=sQuery(id+"F0.wireOp",EDGE,"E11");Q1=makeQuery(id+"F1.opExtrude","CAP_EDGE",EDGE,{"disambiguationData":[OSD([subQ0]),TDD([makeQuery(id+"F0.imprint","IMPRINT",EDGE,{"disambiguationData":[TD([[makeQuery(id+"F0.imprint","INTERSECT",VERTEX,{"disambiguationData":[OD(1.0)],"derivedFrom":[subQ0,sQuery(id+"F0.wireOp",EDGE,"E26.1.3.0")]}),-1.0]])],"derivedFrom":subQ0})])],"isStart":true});}
            var Q2;
            {var subQ0=sQuery(id+"F0.wireOp",EDGE,"E11");Q2=makeQuery(id+"F1.opExtrude","CAP_EDGE",EDGE,{"disambiguationData":[OSD([subQ0]),TDD([makeQuery(id+"F0.imprint","IMPRINT",EDGE,{"disambiguationData":[TD([[makeQuery(id+"F0.imprint","INTERSECT",VERTEX,{"disambiguationData":[OD(1.0)],"derivedFrom":[subQ0,sQuery(id+"F0.wireOp",EDGE,"E25.2.0")]}),-1.0]])],"derivedFrom":subQ0})])],"isStart":true});}
            var Q3;
            {var subQ0=sQuery(id+"F0.wireOp",EDGE,"E11");Q3=makeQuery(id+"F1.opExtrude","CAP_EDGE",EDGE,{"disambiguationData":[OSD([subQ0]),TDD([makeQuery(id+"F0.imprint","IMPRINT",EDGE,{"disambiguationData":[TD([[makeQuery(id+"F0.imprint","INTERSECT",VERTEX,{"disambiguationData":[OD(1.0)],"derivedFrom":[subQ0,sQuery(id+"F0.wireOp",EDGE,"E25.1.0")]}),-1.0]])],"derivedFrom":subQ0})])],"isStart":true});}
            var Q4;
            {var subQ0=sQuery(id+"F0.wireOp",EDGE,"E11");Q4=makeQuery(id+"F1.opExtrude","CAP_EDGE",EDGE,{"disambiguationData":[OSD([subQ0]),TDD([makeQuery(id+"F0.imprint","IMPRINT",EDGE,{"disambiguationData":[TD([[makeQuery(id+"F0.imprint","INTERSECT",VERTEX,{"disambiguationData":[OD(1.0)],"derivedFrom":[subQ0,sQuery(id+"F0.wireOp",EDGE,"E19")]}),-1.0]])],"derivedFrom":subQ0})])],"isStart":true});}
            var Q5;
            {var subQ0=sQuery(id+"F0.wireOp",EDGE,"E11");Q5=makeQuery(id+"F1.opExtrude","CAP_EDGE",EDGE,{"disambiguationData":[OSD([subQ0]),TDD([makeQuery(id+"F0.imprint","IMPRINT",EDGE,{"disambiguationData":[TD([[makeQuery(id+"F0.imprint","INTERSECT",VERTEX,{"disambiguationData":[OD(1.0)],"derivedFrom":[subQ0,sQuery(id+"F0.wireOp",EDGE,"E26.1.8.0")]}),-1.0]])],"derivedFrom":subQ0})])],"isStart":true});}
            var Q6;
            {var subQ0=sQuery(id+"F0.wireOp",EDGE,"E11");Q6=makeQuery(id+"F1.opExtrude","CAP_EDGE",EDGE,{"disambiguationData":[OSD([subQ0]),TDD([makeQuery(id+"F0.imprint","IMPRINT",EDGE,{"disambiguationData":[TD([[makeQuery(id+"F0.imprint","INTERSECT",VERTEX,{"disambiguationData":[OD(1.0)],"derivedFrom":[subQ0,sQuery(id+"F0.wireOp",EDGE,"E26.1.6.0")]}),1.0]])],"derivedFrom":subQ0})])],"isStart":true});}
            var Q7;
            Q7=makeQuery(id+"F1.opExtrude","CAP_EDGE",EDGE,{"disambiguationData":[OSD([sQuery(id+"F0.wireOp",EDGE,"E24")])],"isStart":true});
            var Q8;
            {var subQ0=sQuery(id+"F0.wireOp",EDGE,"E13");Q8=makeQuery(id+"F1.opExtrude","CAP_EDGE",EDGE,{"disambiguationData":[OSD([subQ0]),TDD([makeQuery(id+"F0.imprint","IMPRINT",EDGE,{"disambiguationData":[TD([[makeQuery(id+"F0.imprint","INTERSECT",VERTEX,{"disambiguationData":[OD(1.0)],"derivedFrom":[subQ0,sQuery(id+"F0.wireOp",EDGE,"E17.3.0")]}),-1.0]])],"derivedFrom":subQ0})])],"isStart":true});}
            var Q9;
            {var subQ0=sQuery(id+"F0.wireOp",EDGE,"E13");Q9=makeQuery(id+"F1.opExtrude","CAP_EDGE",EDGE,{"disambiguationData":[OSD([subQ0]),TDD([makeQuery(id+"F0.imprint","IMPRINT",EDGE,{"disambiguationData":[TD([[makeQuery(id+"F0.imprint","INTERSECT",VERTEX,{"disambiguationData":[OD(1.0)],"derivedFrom":[subQ0,sQuery(id+"F0.wireOp",EDGE,"E17.2.0")]}),-1.0]])],"derivedFrom":subQ0})])],"isStart":true});}
            var Q10;
            {var subQ0=sQuery(id+"F0.wireOp",EDGE,"E13");Q10=makeQuery(id+"F1.opExtrude","CAP_EDGE",EDGE,{"disambiguationData":[OSD([subQ0]),TDD([makeQuery(id+"F0.imprint","IMPRINT",EDGE,{"disambiguationData":[TD([[makeQuery(id+"F0.imprint","INTERSECT",VERTEX,{"disambiguationData":[OD(1.0)],"derivedFrom":[subQ0,sQuery(id+"F0.wireOp",EDGE,"E17.1.0")]}),-1.0]])],"derivedFrom":subQ0})])],"isStart":true});}
            var Q11;
            {var subQ0=sQuery(id+"F0.wireOp",EDGE,"E13");Q11=makeQuery(id+"F1.opExtrude","CAP_EDGE",EDGE,{"disambiguationData":[OSD([subQ0]),TDD([makeQuery(id+"F0.imprint","IMPRINT",EDGE,{"disambiguationData":[TD([[makeQuery(id+"F0.imprint","INTERSECT",VERTEX,{"disambiguationData":[OD(0.0)],"derivedFrom":[subQ0,sQuery(id+"F0.wireOp",EDGE,"E17.8.0")]}),1.0]])],"derivedFrom":subQ0})])],"isStart":true});}
            var Q12;
            {var subQ0=sQuery(id+"F0.wireOp",EDGE,"E13");Q12=makeQuery(id+"F1.opExtrude","CAP_EDGE",EDGE,{"disambiguationData":[OSD([subQ0]),TDD([makeQuery(id+"F0.imprint","IMPRINT",EDGE,{"disambiguationData":[TD([[makeQuery(id+"F0.imprint","INTERSECT",VERTEX,{"disambiguationData":[OD(1.0)],"derivedFrom":[subQ0,sQuery(id+"F0.wireOp",EDGE,"E17.8.0")]}),-1.0]])],"derivedFrom":subQ0})])],"isStart":true});}
            var Q13;
            {var subQ0=sQuery(id+"F0.wireOp",EDGE,"E13");Q13=makeQuery(id+"F1.opExtrude","CAP_EDGE",EDGE,{"disambiguationData":[OSD([subQ0]),TDD([makeQuery(id+"F0.imprint","IMPRINT",EDGE,{"disambiguationData":[TD([[makeQuery(id+"F0.imprint","INTERSECT",VERTEX,{"disambiguationData":[OD(1.0)],"derivedFrom":[subQ0,sQuery(id+"F0.wireOp",EDGE,"E17.7.0")]}),-1.0]])],"derivedFrom":subQ0})])],"isStart":true});}
            var Q14;
            Q14=makeQuery(id+"F1.opExtrude","CAP_EDGE",EDGE,{"disambiguationData":[OSD([sQuery(id+"F0.wireOp",EDGE,"E22")])],"isStart":true});
            var Q15;
            {var subQ0=sQuery(id+"F0.wireOp",EDGE,"E10");Q15=makeQuery(id+"F1.opExtrude","CAP_EDGE",EDGE,{"disambiguationData":[OSD([subQ0]),TDD([makeQuery(id+"F0.imprint","IMPRINT",EDGE,{"disambiguationData":[TD([[makeQuery(id+"F0.imprint","INTERSECT",VERTEX,{"disambiguationData":[OD(1.0)],"derivedFrom":[subQ0,sQuery(id+"F0.wireOp",EDGE,"E15.2.0")]}),1.0]])],"derivedFrom":subQ0})])],"isStart":true});}
            var Q16;
            {var subQ0=sQuery(id+"F0.wireOp",EDGE,"E10");Q16=makeQuery(id+"F1.opExtrude","CAP_EDGE",EDGE,{"disambiguationData":[OSD([subQ0]),TDD([makeQuery(id+"F0.imprint","IMPRINT",EDGE,{"disambiguationData":[TD([[makeQuery(id+"F0.imprint","INTERSECT",VERTEX,{"disambiguationData":[OD(0.0)],"derivedFrom":[subQ0,sQuery(id+"F0.wireOp",EDGE,"E15.2.0")]}),-1.0]])],"derivedFrom":subQ0})])],"isStart":true});}
            var Q17;
            {var subQ0=sQuery(id+"F0.wireOp",EDGE,"E10");Q17=makeQuery(id+"F1.opExtrude","CAP_EDGE",EDGE,{"disambiguationData":[OSD([subQ0]),TDD([makeQuery(id+"F0.imprint","IMPRINT",EDGE,{"disambiguationData":[TD([[makeQuery(id+"F0.imprint","INTERSECT",VERTEX,{"disambiguationData":[OD(1.0)],"derivedFrom":[subQ0,sQuery(id+"F0.wireOp",EDGE,"E15.1.0")]}),-1.0]])],"derivedFrom":subQ0})])],"isStart":true});}
            var Q18;
            {var subQ0=sQuery(id+"F0.wireOp",EDGE,"E10");Q18=makeQuery(id+"F1.opExtrude","CAP_EDGE",EDGE,{"disambiguationData":[OSD([subQ0]),TDD([makeQuery(id+"F0.imprint","IMPRINT",EDGE,{"disambiguationData":[TD([[makeQuery(id+"F0.imprint","INTERSECT",VERTEX,{"disambiguationData":[OD(1.0)],"derivedFrom":[subQ0,sQuery(id+"F0.wireOp",EDGE,"E14")]}),-1.0]])],"derivedFrom":subQ0})])],"isStart":true});}
            var Q19;
            {var subQ0=sQuery(id+"F0.wireOp",EDGE,"E10");Q19=makeQuery(id+"F1.opExtrude","CAP_EDGE",EDGE,{"disambiguationData":[OSD([subQ0]),TDD([makeQuery(id+"F0.imprint","IMPRINT",EDGE,{"disambiguationData":[TD([[makeQuery(id+"F0.imprint","INTERSECT",VERTEX,{"disambiguationData":[OD(1.0)],"derivedFrom":[subQ0,sQuery(id+"F0.wireOp",EDGE,"E15.8.0")]}),-1.0]])],"derivedFrom":subQ0})])],"isStart":true});}
            var Q20;
            {var subQ0=sQuery(id+"F0.wireOp",EDGE,"E10");Q20=makeQuery(id+"F1.opExtrude","CAP_EDGE",EDGE,{"disambiguationData":[OSD([subQ0]),TDD([makeQuery(id+"F0.imprint","IMPRINT",EDGE,{"disambiguationData":[TD([[makeQuery(id+"F0.imprint","INTERSECT",VERTEX,{"disambiguationData":[OD(1.0)],"derivedFrom":[subQ0,sQuery(id+"F0.wireOp",EDGE,"E15.7.0")]}),-1.0]])],"derivedFrom":subQ0})])],"isStart":true});}
            var Q21;
            Q21=makeQuery(id+"F1.opExtrude","CAP_EDGE",EDGE,{"disambiguationData":[OSD([sQuery(id+"F0.wireOp",EDGE,"E21")])],"isStart":true});
            var Q22;
            {var subQ0=sQuery(id+"F0.wireOp",EDGE,"E12");Q22=makeQuery(id+"F1.opExtrude","CAP_EDGE",EDGE,{"disambiguationData":[OSD([subQ0]),TDD([makeQuery(id+"F0.imprint","IMPRINT",EDGE,{"disambiguationData":[TD([[makeQuery(id+"F0.imprint","INTERSECT",VERTEX,{"disambiguationData":[OD(1.0)],"derivedFrom":[subQ0,sQuery(id+"F0.wireOp",EDGE,"E20.3.0")]}),-1.0]])],"derivedFrom":subQ0})])],"isStart":true});}
            var Q23;
            {var subQ0=sQuery(id+"F0.wireOp",EDGE,"E12");Q23=makeQuery(id+"F1.opExtrude","CAP_EDGE",EDGE,{"disambiguationData":[OSD([subQ0]),TDD([makeQuery(id+"F0.imprint","IMPRINT",EDGE,{"disambiguationData":[TD([[makeQuery(id+"F0.imprint","INTERSECT",VERTEX,{"disambiguationData":[OD(1.0)],"derivedFrom":[subQ0,sQuery(id+"F0.wireOp",EDGE,"E20.2.0")]}),-1.0]])],"derivedFrom":subQ0})])],"isStart":true});}
            var Q24;
            {var subQ0=sQuery(id+"F0.wireOp",EDGE,"E12");Q24=makeQuery(id+"F1.opExtrude","CAP_EDGE",EDGE,{"disambiguationData":[OSD([subQ0]),TDD([makeQuery(id+"F0.imprint","IMPRINT",EDGE,{"disambiguationData":[TD([[makeQuery(id+"F0.imprint","INTERSECT",VERTEX,{"disambiguationData":[OD(1.0)],"derivedFrom":[subQ0,sQuery(id+"F0.wireOp",EDGE,"E20.1.0")]}),-1.0]])],"derivedFrom":subQ0})])],"isStart":true});}
            var Q25;
            {var subQ0=sQuery(id+"F0.wireOp",EDGE,"E12");Q25=makeQuery(id+"F1.opExtrude","CAP_EDGE",EDGE,{"disambiguationData":[OSD([subQ0]),TDD([makeQuery(id+"F0.imprint","IMPRINT",EDGE,{"disambiguationData":[TD([[makeQuery(id+"F0.imprint","INTERSECT",VERTEX,{"disambiguationData":[OD(1.0)],"derivedFrom":[subQ0,sQuery(id+"F0.wireOp",EDGE,"E18")]}),-1.0]])],"derivedFrom":subQ0})])],"isStart":true});}
            var Q26;
            {var subQ0=sQuery(id+"F0.wireOp",EDGE,"E12");Q26=makeQuery(id+"F1.opExtrude","CAP_EDGE",EDGE,{"disambiguationData":[OSD([subQ0]),TDD([makeQuery(id+"F0.imprint","IMPRINT",EDGE,{"disambiguationData":[TD([[makeQuery(id+"F0.imprint","INTERSECT",VERTEX,{"disambiguationData":[OD(1.0)],"derivedFrom":[subQ0,sQuery(id+"F0.wireOp",EDGE,"E20.7.0")]}),-1.0]])],"derivedFrom":subQ0})])],"isStart":true});}
            var Q27;
            {var subQ0=sQuery(id+"F0.wireOp",EDGE,"E12");Q27=makeQuery(id+"F1.opExtrude","CAP_EDGE",EDGE,{"disambiguationData":[OSD([subQ0]),TDD([makeQuery(id+"F0.imprint","IMPRINT",EDGE,{"disambiguationData":[TD([[makeQuery(id+"F0.imprint","INTERSECT",VERTEX,{"disambiguationData":[OD(1.0)],"derivedFrom":[subQ0,sQuery(id+"F0.wireOp",EDGE,"E20.8.0")]}),-1.0]])],"derivedFrom":subQ0})])],"isStart":true});}
            fillet(context, id + "F3", {"entities" : qUnion([Q0, Q1, Q2, Q3, Q4, Q5, Q6, Q7, Q8, Q9, Q10, Q11, Q12, Q13, Q14, Q15, Q16, Q17, Q18, Q19, Q20, Q21, Q22, Q23, Q24, Q25, Q26, Q27]), "radius" : 1.27 * mm, "tangentPropagation" : true, "allowEdgeOverflow" : false});
        }
    });
